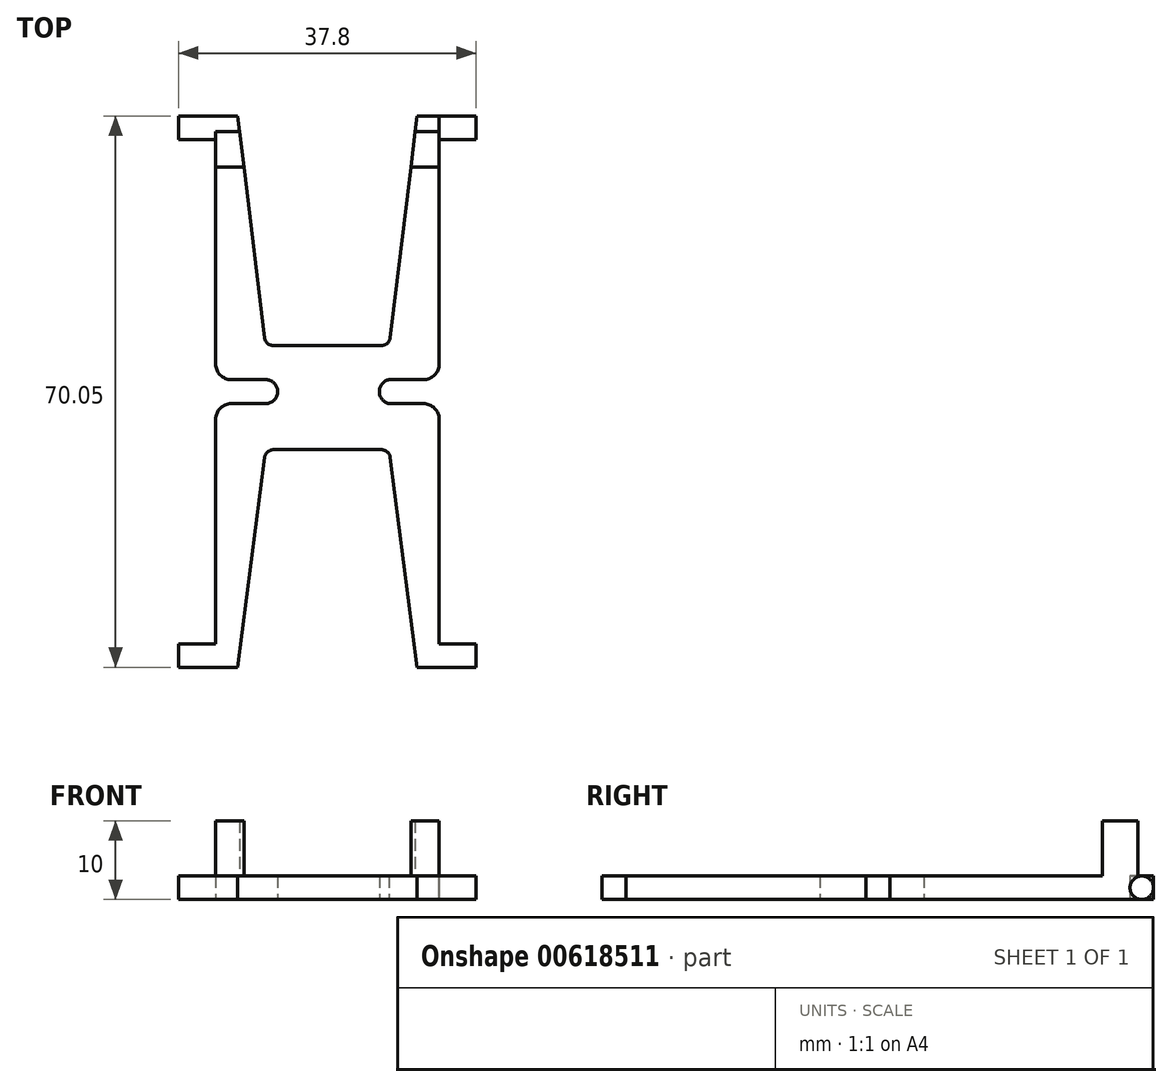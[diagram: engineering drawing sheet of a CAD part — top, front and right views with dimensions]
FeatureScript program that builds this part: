
annotation { "Feature Type Name" : "Feature", "Feature Type Description" : "" }
export const myFeature = defineFeature(function(context is Context, id is Id, definition is map)
    precondition{}
    {
        {
            var Q0;
            Q0=qCreatedBy(makeId("Top.planeOp"),FACE);
            var sketch = newSketch(context, id + "F0", { "sketchPlane" : qUnion([Q0])});
            skLineSegment(sketch, "E0", {"start": v(-21.67, 33.49) * mm, "end": v(-14.17, 33.49) * mm, "construction": true});
            skLineSegment(sketch, "E1", {"start": v(16.13, 33.49) * mm, "end": v(8.63, 33.49) * mm, "construction": true});
            skLineSegment(sketch, "E2", {"start": v(16.13, 30.49) * mm, "end": v(11.43, 30.49) * mm, "construction": true});
            skLineSegment(sketch, "E3", {"start": v(-21.67, 33.49) * mm, "end": v(-21.67, 30.49) * mm, "construction": true});
            skLineSegment(sketch, "E4", {"start": v(-21.67, 30.49) * mm, "end": v(-16.97, 30.49) * mm, "construction": true});
            skLineSegment(sketch, "E5", {"start": v(-16.97, 30.49) * mm, "end": v(-16.97, -0.01) * mm, "construction": true});
            skLineSegment(sketch, "E6", {"start": v(11.43, 30.49) * mm, "end": v(11.43, -0.01) * mm, "construction": true});
            skLineSegment(sketch, "E7", {"start": v(-21.67, -36.56) * mm, "end": v(-21.67, -33.56) * mm, "construction": true});
            skLineSegment(sketch, "E8", {"start": v(-21.67, -33.56) * mm, "end": v(-16.97, -33.56) * mm, "construction": true});
            skLineSegment(sketch, "E9", {"start": v(16.13, -36.56) * mm, "end": v(16.13, -33.56) * mm, "construction": true});
            skLineSegment(sketch, "E10", {"start": v(16.13, -33.56) * mm, "end": v(11.43, -33.56) * mm, "construction": true});
            skLineSegment(sketch, "E11", {"start": v(16.13, -36.56) * mm, "end": v(8.63, -36.56) * mm, "construction": true});
            skLineSegment(sketch, "E12", {"start": v(-21.67, -36.56) * mm, "end": v(-14.17, -36.56) * mm, "construction": true});
            skLineSegment(sketch, "E13", {"start": v(-16.97, -33.56) * mm, "end": v(-16.97, -3.06) * mm, "construction": true});
            skLineSegment(sketch, "E14", {"start": v(11.43, -33.56) * mm, "end": v(11.43, -3.06) * mm, "construction": true});
            skLineSegment(sketch, "E15", {"start": v(-16.97, -15.75) * mm, "end": v(11.43, -15.75) * mm, "construction": true});
            skLineSegment(sketch, "E16", {"start": v(16.13, -33.56) * mm, "end": v(11.43, -33.56) * mm});
            skLineSegment(sketch, "E17", {"start": v(11.43, -5.06) * mm, "end": v(11.43, -33.56) * mm});
            skLineSegment(sketch, "E18", {"start": v(-21.67, -36.56) * mm, "end": v(-21.67, -33.56) * mm});
            skLineSegment(sketch, "E19", {"start": v(-21.67, -33.56) * mm, "end": v(-16.97, -33.56) * mm});
            skLineSegment(sketch, "E20", {"start": v(-16.97, -33.56) * mm, "end": v(-16.97, -5.06) * mm});
            skLineSegment(sketch, "E21", {"start": v(-16.97, 1.99) * mm, "end": v(-16.97, 30.49) * mm});
            skLineSegment(sketch, "E22", {"start": v(-16.97, 30.49) * mm, "end": v(-21.67, 30.49) * mm});
            skLineSegment(sketch, "E23", {"start": v(-21.67, 30.49) * mm, "end": v(-21.67, 33.49) * mm});
            skLineSegment(sketch, "E24", {"start": v(16.13, 33.49) * mm, "end": v(16.13, 30.49) * mm});
            skLineSegment(sketch, "E25", {"start": v(16.13, 30.49) * mm, "end": v(11.43, 30.49) * mm});
            skLineSegment(sketch, "E26", {"start": v(11.43, 30.49) * mm, "end": v(11.43, 1.99) * mm});
            skLineSegment(sketch, "E27", {"start": v(-14.97, -3.06) * mm, "end": v(-10.62, -3.06) * mm});
            skLineSegment(sketch, "E28", {"start": v(-14.97, -0.01) * mm, "end": v(-10.62, -0.01) * mm});
            skLineSegment(sketch, "E29", {"start": v(9.43, -3.06) * mm, "end": v(5.08, -3.06) * mm});
            skLineSegment(sketch, "E30", {"start": v(9.43, -0.01) * mm, "end": v(5.08, -0.01) * mm});
            skLineSegment(sketch, "E31", {"start": v(-10.62, -0.01) * mm, "end": v(5.08, -3.06) * mm, "construction": true});
            skLineSegment(sketch, "E32", {"start": v(-2.77, -1.54) * mm, "end": v(-2.77, 4.31) * mm, "construction": true});
            skLineSegment(sketch, "E33", {"start": v(-2.77, -1.54) * mm, "end": v(-2.77, -7.39) * mm, "construction": true});
            skLineSegment(sketch, "E34", {"start": v(-2.77, 4.31) * mm, "end": v(-10.62, 4.31) * mm, "construction": true});
            skLineSegment(sketch, "E35", {"start": v(-10.62, -3.06) * mm, "end": v(-10.62, -8.91) * mm, "construction": true});
            skLineSegment(sketch, "E36", {"start": v(-21.67, -36.56) * mm, "end": v(-14.17, -36.56) * mm});
            skLineSegment(sketch, "E37", {"start": v(8.63, -36.56) * mm, "end": v(16.13, -36.56) * mm});
            skLineSegment(sketch, "E38", {"start": v(16.13, -33.56) * mm, "end": v(16.13, -36.56) * mm});
            skLineSegment(sketch, "E39", {"start": v(-14.17, 33.49) * mm, "end": v(-21.67, 33.49) * mm});
            skLineSegment(sketch, "E40", {"start": v(8.63, 33.49) * mm, "end": v(16.13, 33.49) * mm});
            skPoint(sketch, "E41.visualSharp", {"position": v(-10.62, 4.31) * mm});
            skLineSegment(sketch, "E41.filletArc", {"start": v(-10.62, 4.31) * mm, "end": v(-10.62, 4.31) * mm});
            skPoint(sketch, "E42.visualSharp", {"position": v(5.08, 4.31) * mm});
            skLineSegment(sketch, "E42.filletArc", {"start": v(5.08, 4.31) * mm, "end": v(5.08, 4.31) * mm});
            skPoint(sketch, "E43.visualSharp", {"position": v(5.08, -8.91) * mm});
            skLineSegment(sketch, "E43.filletArc", {"start": v(5.08, -8.91) * mm, "end": v(5.08, -8.91) * mm});
            skPoint(sketch, "E44.visualSharp", {"position": v(-10.62, -8.91) * mm});
            skLineSegment(sketch, "E44.filletArc", {"start": v(-10.62, -8.91) * mm, "end": v(-10.62, -8.91) * mm});
            skPoint(sketch, "E45.visualSharp", {"position": v(-10.62, -3.06) * mm});
            skLineSegment(sketch, "E45.filletArc", {"start": v(-10.62, -3.06) * mm, "end": v(-10.62, -3.06) * mm});
            skPoint(sketch, "E46.visualSharp", {"position": v(11.43, -0.01) * mm});
            skArc(sketch, "E46.filletArc", {"start": v(9.43, -0.01) * mm, "mid": v(10.85, 0.57) * mm, "end": v(11.43, 1.99) * mm});
            skPoint(sketch, "E47.visualSharp", {"position": v(11.43, -3.06) * mm});
            skArc(sketch, "E47.filletArc", {"start": v(11.43, -5.06) * mm, "mid": v(10.85, -3.65) * mm, "end": v(9.43, -3.06) * mm});
            skPoint(sketch, "E48.visualSharp", {"position": v(-16.97, -0.01) * mm});
            skArc(sketch, "E48.filletArc", {"start": v(-16.97, 1.99) * mm, "mid": v(-16.38, 0.57) * mm, "end": v(-14.97, -0.01) * mm});
            skPoint(sketch, "E49.visualSharp", {"position": v(-16.97, -3.06) * mm});
            skArc(sketch, "E49.filletArc", {"start": v(-14.97, -3.06) * mm, "mid": v(-16.38, -3.65) * mm, "end": v(-16.97, -5.06) * mm});
            skArc(sketch, "E50", {"start": v(5.08, -0.01) * mm, "mid": v(3.83, -1.54) * mm, "end": v(5.08, -3.06) * mm});
            skArc(sketch, "E51", {"start": v(-10.62, -3.06) * mm, "mid": v(-9.1, -1.54) * mm, "end": v(-10.62, -0.01) * mm});
            skLineSegment(sketch, "E52", {"start": v(-10.62, -8.91) * mm, "end": v(-10.74, -9.9) * mm, "construction": true});
            skArc(sketch, "E53", {"start": v(-9.62, -8.91) * mm, "mid": v(-10.37, -9.2) * mm, "end": v(-10.74, -9.9) * mm});
            skArc(sketch, "E54", {"start": v(5.21, -9.9) * mm, "mid": v(4.84, -9.2) * mm, "end": v(4.08, -8.91) * mm});
            skLineSegment(sketch, "E55", {"start": v(-10.74, -9.9) * mm, "end": v(-14.17, -36.56) * mm});
            skLineSegment(sketch, "E56", {"start": v(8.63, -36.56) * mm, "end": v(5.21, -9.9) * mm});
            skLineSegment(sketch, "E57", {"start": v(4.08, -8.91) * mm, "end": v(-9.62, -8.91) * mm});
            skLineSegment(sketch, "E58", {"start": v(5.08, 4.31) * mm, "end": v(5.2, 5.3) * mm, "construction": true});
            skLineSegment(sketch, "E59", {"start": v(5.08, 4.31) * mm, "end": v(4.08, 4.31) * mm, "construction": true});
            skLineSegment(sketch, "E60", {"start": v(-10.62, 4.31) * mm, "end": v(-9.62, 4.31) * mm, "construction": true});
            skLineSegment(sketch, "E61", {"start": v(-10.62, 4.31) * mm, "end": v(-10.74, 5.3) * mm, "construction": true});
            skArc(sketch, "E62", {"start": v(-10.74, 5.3) * mm, "mid": v(-10.36, 4.6) * mm, "end": v(-9.62, 4.31) * mm});
            skArc(sketch, "E63", {"start": v(4.08, 4.31) * mm, "mid": v(4.83, 4.6) * mm, "end": v(5.2, 5.3) * mm});
            skLineSegment(sketch, "E64", {"start": v(5.2, 5.3) * mm, "end": v(8.63, 33.49) * mm});
            skLineSegment(sketch, "E65", {"start": v(-14.17, 33.49) * mm, "end": v(-10.74, 5.3) * mm});
            skLineSegment(sketch, "E66", {"start": v(-9.62, 4.31) * mm, "end": v(4.08, 4.31) * mm});
            skSolve(sketch);
        }
        {
            var Q0;
            Q0 = qSketchRegion(id + "F0", true);
            extrude(context, id + "F1", {"entities" : qUnion([Q0]), "depth" : 3 * mm, "offsetDistance" : 25 * mm});
        }
        {
            var Q0;
            Q0=makeQuery(id+"F1.opExtrude","CAP_FACE",FACE,{"disambiguationData":[OSD([sQuery(id+"F0.wireOp",EDGE,"E16"),sQuery(id+"F0.wireOp",EDGE,"E17"),sQuery(id+"F0.wireOp",EDGE,"E18"),sQuery(id+"F0.wireOp",EDGE,"E19"),sQuery(id+"F0.wireOp",EDGE,"E20"),sQuery(id+"F0.wireOp",EDGE,"E21"),sQuery(id+"F0.wireOp",EDGE,"E22"),sQuery(id+"F0.wireOp",EDGE,"E23"),sQuery(id+"F0.wireOp",EDGE,"E24"),sQuery(id+"F0.wireOp",EDGE,"E25"),sQuery(id+"F0.wireOp",EDGE,"E26"),sQuery(id+"F0.wireOp",EDGE,"E27"),sQuery(id+"F0.wireOp",EDGE,"E28"),sQuery(id+"F0.wireOp",EDGE,"E29"),sQuery(id+"F0.wireOp",EDGE,"E30"),sQuery(id+"F0.wireOp",EDGE,"E36"),sQuery(id+"F0.wireOp",EDGE,"E37"),sQuery(id+"F0.wireOp",EDGE,"E38"),sQuery(id+"F0.wireOp",EDGE,"E39"),sQuery(id+"F0.wireOp",EDGE,"E40"),sQuery(id+"F0.wireOp",EDGE,"E46.filletArc"),sQuery(id+"F0.wireOp",EDGE,"E47.filletArc"),sQuery(id+"F0.wireOp",EDGE,"E48.filletArc"),sQuery(id+"F0.wireOp",EDGE,"E49.filletArc"),sQuery(id+"F0.wireOp",EDGE,"E50"),sQuery(id+"F0.wireOp",EDGE,"E51"),sQuery(id+"F0.wireOp",EDGE,"E53"),sQuery(id+"F0.wireOp",EDGE,"E54"),sQuery(id+"F0.wireOp",EDGE,"E55"),sQuery(id+"F0.wireOp",EDGE,"E56"),sQuery(id+"F0.wireOp",EDGE,"E57"),sQuery(id+"F0.wireOp",EDGE,"E62"),sQuery(id+"F0.wireOp",EDGE,"E63"),sQuery(id+"F0.wireOp",EDGE,"E64"),sQuery(id+"F0.wireOp",EDGE,"E65"),sQuery(id+"F0.wireOp",EDGE,"E66")])],"isStart":false});
            var sketch = newSketch(context, id + "F2", { "sketchPlane" : qUnion([Q0])});
            skLineSegment(sketch, "E67", {"start": v(-16.97, 30.49) * mm, "end": v(-16.97, 26.99) * mm, "construction": true});
            skLineSegment(sketch, "E68", {"start": v(11.43, 30.49) * mm, "end": v(11.43, 26.99) * mm, "construction": true});
            skLineSegment(sketch, "E69", {"start": v(11.43, 30.49) * mm, "end": v(11.43, 31.49) * mm, "construction": true});
            skLineSegment(sketch, "E70", {"start": v(-16.97, 30.49) * mm, "end": v(-16.97, 31.49) * mm, "construction": true});
            skLineSegment(sketch, "E71", {"start": v(-16.97, 31.49) * mm, "end": v(-13.92, 31.49) * mm});
            skLineSegment(sketch, "E72", {"start": v(-13.92, 31.49) * mm, "end": v(-13.37, 26.99) * mm});
            skLineSegment(sketch, "E73", {"start": v(-13.37, 26.99) * mm, "end": v(-16.97, 26.99) * mm});
            skLineSegment(sketch, "E74", {"start": v(-16.97, 31.49) * mm, "end": v(-16.97, 26.99) * mm});
            skLineSegment(sketch, "E75", {"start": v(11.43, 31.49) * mm, "end": v(11.43, 26.99) * mm});
            skLineSegment(sketch, "E76", {"start": v(11.43, 26.99) * mm, "end": v(7.84, 26.99) * mm});
            skLineSegment(sketch, "E77", {"start": v(11.43, 31.49) * mm, "end": v(8.4, 31.49) * mm});
            skLineSegment(sketch, "E78", {"start": v(7.84, 26.99) * mm, "end": v(8.4, 31.49) * mm});
            skSolve(sketch);
        }
        {
            var Q0;
            Q0 = qSketchRegion(id + "F2", true);
            extrude(context, id + "F3", {"entities" : qUnion([Q0]), "operationType" : NewBodyOperationType.ADD, "depth" : 7 * mm, "offsetDistance" : 25 * mm});
        }
        {
            var Q0;
            Q0=makeQuery(id+"F1.opExtrude","SWEPT_FACE",FACE,{"disambiguationData":[OSD([sQuery(id+"F0.wireOp",EDGE,"E24")])]});
            var sketch = newSketch(context, id + "F4", { "sketchPlane" : qUnion([Q0])});
            skLineSegment(sketch, "E79", {"start": v(33.49, 3) * mm, "end": v(30.49, 0) * mm, "construction": true});
            skCircle(sketch, "E80", {"center": v(31.99, 1.5) * mm, "radius": 1.5 * mm});
            skSolve(sketch);
        }
        {
            var Q0;
            {var subQ0=sQuery(id+"F4.wireOp",EDGE,"E80");var subQ1=sQuery(id+"F0.wireOp",EDGE,"E24");var subQ2=makeQuery(id+"F1.opExtrude","CAP_EDGE",EDGE,{"disambiguationData":[OSD([subQ1])],"isStart":false});var subQ3=makeQuery(id+"F4.imprint","INTERSECT",VERTEX,{"derivedFrom":[subQ2,subQ0]});Q0=makeQuery(id+"F4.imprint","IMPRINT",FACE,{"disambiguationData":[TD([[makeQuery(id+"F4.imprint","IMPRINT",EDGE,{"disambiguationData":[TD([[subQ3,1.0]])],"derivedFrom":subQ0}),-1.0]])]});}
            var Q1;
            {var subQ0=sQuery(id+"F4.wireOp",EDGE,"E80");var subQ1=sQuery(id+"F0.wireOp",EDGE,"E24");var subQ4=makeQuery(id+"F1.opExtrude","CAP_EDGE",EDGE,{"disambiguationData":[OSD([subQ1])],"isStart":true});var subQ5=makeQuery(id+"F4.imprint","INTERSECT",VERTEX,{"derivedFrom":[subQ4,subQ0]});Q1=makeQuery(id+"F4.imprint","IMPRINT",FACE,{"disambiguationData":[TD([[makeQuery(id+"F4.imprint","IMPRINT",EDGE,{"disambiguationData":[TD([[subQ5,-1.0]])],"derivedFrom":subQ0}),-1.0]])]});}
            var Q2;
            {var subQ0=sQuery(id+"F4.wireOp",EDGE,"E80");var subQ1=sQuery(id+"F0.wireOp",EDGE,"E24");var subQ4=makeQuery(id+"F1.opExtrude","CAP_EDGE",EDGE,{"disambiguationData":[OSD([subQ1])],"isStart":true});var subQ5=makeQuery(id+"F4.imprint","INTERSECT",VERTEX,{"derivedFrom":[subQ4,subQ0]});Q2=makeQuery(id+"F4.imprint","IMPRINT",FACE,{"disambiguationData":[TD([[makeQuery(id+"F4.imprint","IMPRINT",EDGE,{"disambiguationData":[TD([[subQ5,1.0]])],"derivedFrom":subQ0}),-1.0]])]});}
            var Q3;
            {var subQ0=sQuery(id+"F4.wireOp",EDGE,"E80");var subQ1=sQuery(id+"F0.wireOp",EDGE,"E24");var subQ2=makeQuery(id+"F1.opExtrude","CAP_EDGE",EDGE,{"disambiguationData":[OSD([subQ1])],"isStart":false});var subQ3=makeQuery(id+"F4.imprint","INTERSECT",VERTEX,{"derivedFrom":[subQ2,subQ0]});Q3=makeQuery(id+"F4.imprint","IMPRINT",FACE,{"disambiguationData":[TD([[makeQuery(id+"F4.imprint","IMPRINT",EDGE,{"disambiguationData":[TD([[subQ3,-1.0]])],"derivedFrom":subQ0}),-1.0]])]});}
            extrude(context, id + "F5", {"entities" : qUnion([Q0, Q1, Q2, Q3]), "operationType" : NewBodyOperationType.REMOVE, "oppositeDirection" : true, "depth" : 4.7 * mm, "offsetDistance" : 25 * mm});
        }
    });
